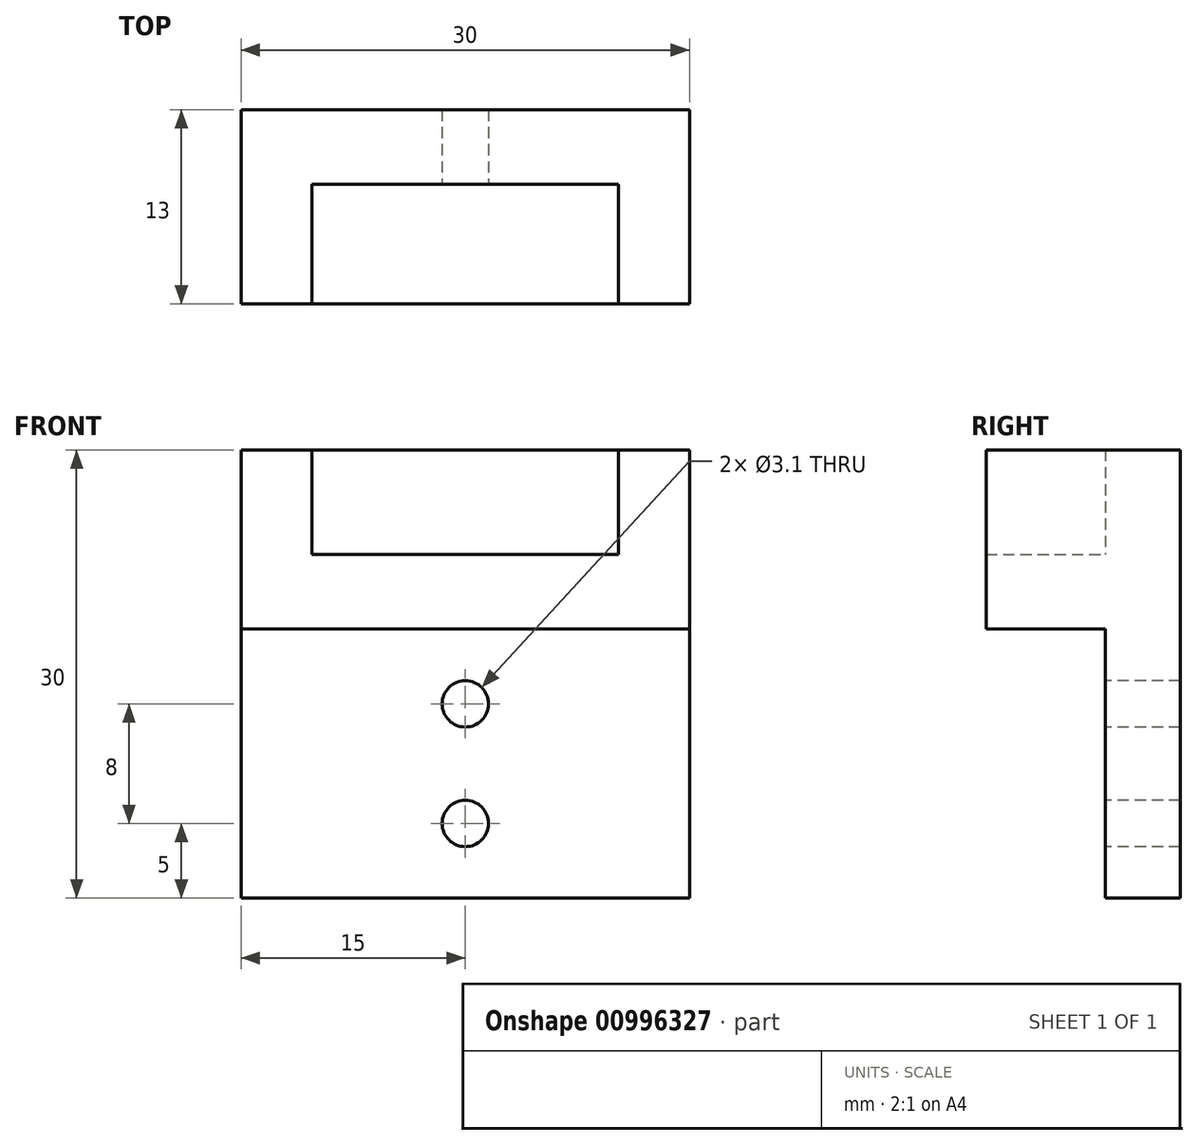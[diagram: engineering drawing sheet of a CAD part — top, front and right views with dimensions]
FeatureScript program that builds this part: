
annotation { "Feature Type Name" : "Feature", "Feature Type Description" : "" }
export const myFeature = defineFeature(function(context is Context, id is Id, definition is map)
    precondition{}
    {
        {
            var Q0;
            Q0=qCreatedBy(makeId("Front.planeOp"),FACE);
            var sketch = newSketch(context, id + "F0", { "sketchPlane" : qUnion([Q0])});
            skLineSegment(sketch, "E0.bottom", {"start": v(-15, 15) * mm, "end": v(15, 15) * mm});
            skLineSegment(sketch, "E0.top", {"start": v(-15, -15) * mm, "end": v(15, -15) * mm});
            skLineSegment(sketch, "E0.left", {"start": v(-15, 15) * mm, "end": v(-15, -15) * mm});
            skLineSegment(sketch, "E0.right", {"start": v(15, 15) * mm, "end": v(15, -15) * mm});
            skPoint(sketch, "E0.middle", {"position": v(0, 0) * mm});
            skSolve(sketch);
        }
        {
            var Q0;
            Q0 = qSketchRegion(id + "F0", true);
            extrude(context, id + "F1", {"entities" : qUnion([Q0]), "depth" : 5 * mm, "offsetDistance" : 25 * mm});
        }
        {
            var Q0;
            Q0=makeQuery(id+"F1.opExtrude","CAP_FACE",FACE,{"disambiguationData":[OSD([sQuery(id+"F0.wireOp",EDGE,"E0.bottom"),sQuery(id+"F0.wireOp",EDGE,"E0.top"),sQuery(id+"F0.wireOp",EDGE,"E0.left"),sQuery(id+"F0.wireOp",EDGE,"E0.right")])],"isStart":true});
            var sketch = newSketch(context, id + "F2", { "sketchPlane" : qUnion([Q0])});
            skLineSegment(sketch, "E1.bottom", {"start": v(-10.25, 15) * mm, "end": v(10.25, 15) * mm});
            skLineSegment(sketch, "E1.top", {"start": v(-10.25, -15) * mm, "end": v(10.25, -15) * mm});
            skLineSegment(sketch, "E1.left", {"start": v(-10.25, 15) * mm, "end": v(-10.25, -15) * mm});
            skLineSegment(sketch, "E1.right", {"start": v(10.25, 15) * mm, "end": v(10.25, -15) * mm});
            skPoint(sketch, "E1.middle", {"position": v(0, 0) * mm});
            skSolve(sketch);
        }
        {
            var Q0;
            Q0=makeQuery(id+"F1.opExtrude","CAP_FACE",FACE,{"disambiguationData":[OSD([sQuery(id+"F0.wireOp",EDGE,"E0.bottom"),sQuery(id+"F0.wireOp",EDGE,"E0.top"),sQuery(id+"F0.wireOp",EDGE,"E0.left"),sQuery(id+"F0.wireOp",EDGE,"E0.right")])],"isStart":false});
            var sketch = newSketch(context, id + "F3", { "sketchPlane" : qUnion([Q0])});
            skLineSegment(sketch, "E2.bottom", {"start": v(-10.25, 15) * mm, "end": v(10.25, 15) * mm});
            skLineSegment(sketch, "E2.top", {"start": v(-10.25, -15) * mm, "end": v(10.25, -15) * mm});
            skLineSegment(sketch, "E2.left", {"start": v(-10.25, 15) * mm, "end": v(-10.25, -15) * mm});
            skLineSegment(sketch, "E2.right", {"start": v(10.25, 15) * mm, "end": v(10.25, -15) * mm});
            skPoint(sketch, "E2.middle", {"position": v(0, 0) * mm});
            skLineSegment(sketch, "E3", {"start": v(-10.25, 15) * mm, "end": v(-10.25, 8) * mm});
            skLineSegment(sketch, "E4", {"start": v(-10.25, 8) * mm, "end": v(10.25, 8) * mm});
            skLineSegment(sketch, "E5", {"start": v(10.25, 8) * mm, "end": v(10.25, 3) * mm});
            skLineSegment(sketch, "E6", {"start": v(10.25, 3) * mm, "end": v(-10.25, 3) * mm});
            skLineSegment(sketch, "E7", {"start": v(-10.25, 3) * mm, "end": v(-15, 3) * mm});
            skLineSegment(sketch, "E8", {"start": v(-15, 3) * mm, "end": v(15, 3) * mm});
            skSolve(sketch);
        }
        {
            var Q0;
            {var subQ5=sQuery(id+"F3.wireOp",EDGE,"E7");Q0=makeQuery(id+"F3.imprint","IMPRINT",FACE,{"disambiguationData":[TD([[makeQuery(id+"F3.imprint","IMPRINT",EDGE,{"derivedFrom":subQ5}),-1.0]])]});}
            var Q1;
            {var subQ2=sQuery(id+"F3.wireOp",EDGE,"E4");Q1=makeQuery(id+"F3.imprint","IMPRINT",FACE,{"disambiguationData":[TD([[makeQuery(id+"F3.imprint","IMPRINT",EDGE,{"derivedFrom":subQ2}),-1.0]])]});}
            var Q2;
            {var subQ5=sQuery(id+"F3.wireOp",EDGE,"E8");Q2=makeQuery(id+"F3.imprint","IMPRINT",FACE,{"disambiguationData":[TD([[makeQuery(id+"F3.imprint","IMPRINT",EDGE,{"derivedFrom":subQ5}),1.0]])]});}
            extrude(context, id + "F4", {"entities" : qUnion([Q0, Q1, Q2]), "operationType" : NewBodyOperationType.ADD, "depth" : 8 * mm, "offsetDistance" : 25 * mm});
        }
        {
            var Q0;
            {var subQ0=sQuery(id+"F0.wireOp",EDGE,"E0.top");var subQ1=sQuery(id+"F0.wireOp",EDGE,"E0.right");var subQ2=sQuery(id+"F0.wireOp",EDGE,"E0.left");Q0=makeQuery(id+"F4.boolean.opBoolean","SPLIT",FACE,{"disambiguationData":[TD([makeQuery(id+"F1.opExtrude","SWEPT_FACE",FACE,{"disambiguationData":[OSD([subQ0])]})])],"derivedFrom":makeQuery(id+"F1.opExtrude","CAP_FACE",FACE,{"disambiguationData":[OSD([sQuery(id+"F0.wireOp",EDGE,"E0.bottom"),subQ0,subQ2,subQ1])],"isStart":false})});}
            var sketch = newSketch(context, id + "F5", { "sketchPlane" : qUnion([Q0])});
            skLineSegment(sketch, "E9", {"start": v(0, 3) * mm, "end": v(0, -2) * mm});
            skLineSegment(sketch, "E10", {"start": v(0, -2) * mm, "end": v(0, -10) * mm});
            skCircle(sketch, "E11", {"center": v(0, -2) * mm, "radius": 1.55 * mm});
            skCircle(sketch, "E12", {"center": v(0, -10) * mm, "radius": 1.55 * mm});
            skSolve(sketch);
        }
        {
            var Q0;
            {var subQ0=sQuery(id+"F5.wireOp",EDGE,"E10");var subQ1=sQuery(id+"F5.wireOp",EDGE,"E9");var subQ2=makeQuery(id+"F5.imprint","INTERSECT",VERTEX,{"derivedFrom":[subQ1,subQ0]});Q0=makeQuery(id+"F5.imprint","IMPRINT",FACE,{"disambiguationData":[TD([[makeQuery(id+"F5.imprint","IMPRINT",EDGE,{"disambiguationData":[TD([[subQ2,1.0]])],"derivedFrom":subQ1}),-1.0]])]});}
            var Q1;
            {var subQ0=sQuery(id+"F5.wireOp",EDGE,"E10");var subQ1=sQuery(id+"F5.wireOp",EDGE,"E9");var subQ2=makeQuery(id+"F5.imprint","INTERSECT",VERTEX,{"derivedFrom":[subQ1,subQ0]});Q1=makeQuery(id+"F5.imprint","IMPRINT",FACE,{"disambiguationData":[TD([[makeQuery(id+"F5.imprint","IMPRINT",EDGE,{"disambiguationData":[TD([[subQ2,1.0]])],"derivedFrom":subQ1}),1.0]])]});}
            var Q2;
            Q2=makeQuery(id+"F5.imprint","IMPRINT",FACE,{"disambiguationData":[TD([[makeQuery(id+"F5.imprint","IMPRINT",EDGE,{"derivedFrom":sQuery(id+"F5.wireOp",EDGE,"E12")}),1.0]])]});
            extrude(context, id + "F6", {"entities" : qUnion([Q0, Q1, Q2]), "operationType" : NewBodyOperationType.REMOVE, "oppositeDirection" : true, "depth" : 25 * mm, "offsetDistance" : 25 * mm});
        }
    });
